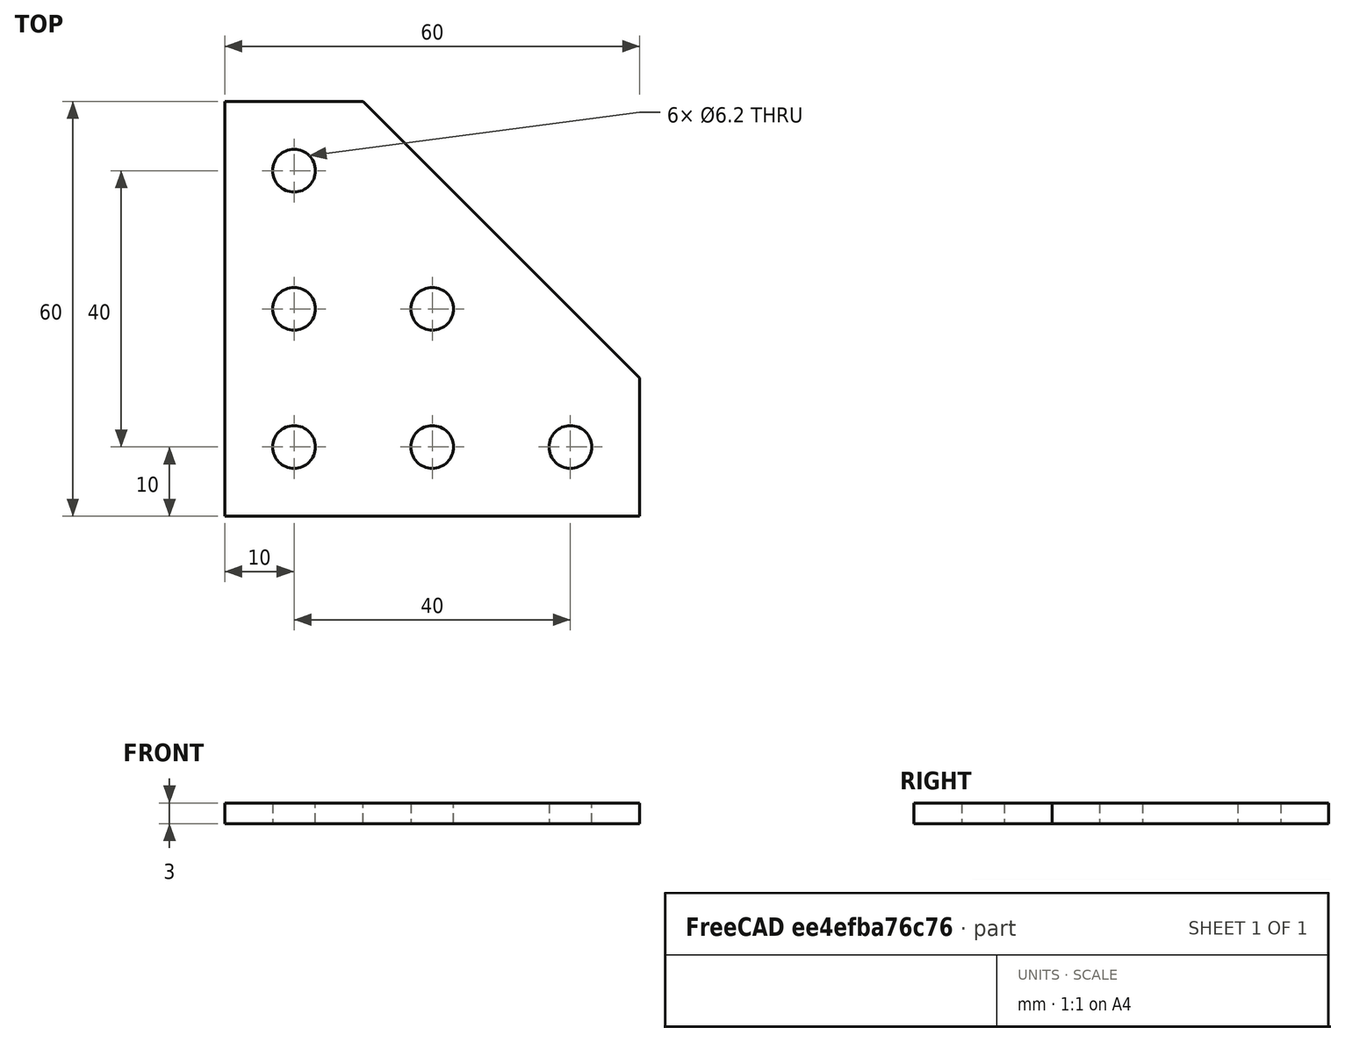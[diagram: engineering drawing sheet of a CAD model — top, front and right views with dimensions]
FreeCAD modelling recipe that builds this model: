
FCSTD DOCUMENT  (FreeCAD 0.17R9796 (Git))
Label: lcon
License: All rights reserved
LicenseURL: http://en.wikipedia.org/wiki/All_rights_reserved
objects: Sketcher::SketchObject×1, PartDesign::Pad×1, PartDesign::Body×1
note: 4 computed .brp shape members not serialized (recipe doc carries the construction recipe); baked Part::Feature solids carry a one-line shape summary decoded from their .brp

FEATURE [Sketcher::SketchObject] Sketch
  MapMode = 5
  Support = -> [XY_Plane]
  sketch-geometry (11):
    g0: LineSegment StartX=0 StartY=60 StartZ=0 EndX=20 EndY=60 EndZ=0
    g1: LineSegment StartX=20 StartY=60 StartZ=0 EndX=60 EndY=20 EndZ=0
    g2: LineSegment StartX=60 StartY=20 StartZ=0 EndX=60 EndY=0 EndZ=0
    g3: LineSegment StartX=60 StartY=0 StartZ=0 EndX=0 EndY=0 EndZ=0
    g4: LineSegment StartX=0 StartY=0 StartZ=0 EndX=0 EndY=60 EndZ=0
    g5: Circle CenterX=10 CenterY=10 CenterZ=0 NormalX=0 NormalY=0 NormalZ=1 Radius=3.1
    g6: Circle CenterX=10 CenterY=30 CenterZ=0 NormalX=0 NormalY=0 NormalZ=1 Radius=3.1
    g7: Circle CenterX=10 CenterY=50 CenterZ=0 NormalX=0 NormalY=0 NormalZ=1 Radius=3.1
    g8: Circle CenterX=30 CenterY=10 CenterZ=0 NormalX=0 NormalY=0 NormalZ=1 Radius=3.1
    g9: Circle CenterX=50 CenterY=10 CenterZ=0 NormalX=0 NormalY=0 NormalZ=1 Radius=3.1
    g10: Circle CenterX=30 CenterY=30 CenterZ=0 NormalX=0 NormalY=0 NormalZ=1 Radius=3.1
  constraints (32):
    c: Coincident(g0,g1)
    c: Coincident(g1,g2)
    c: Coincident(g2,g3)
    c: Coincident(g3,g4)
    c: Coincident(g4,g0)
    c: Coincident(g3,g-1)
    c: DistanceX(g-1,g2) = 60
    c: DistanceY(g-1,g0) = 60
    c: DistanceX(g-1,g1) = 60
    c: DistanceX(g-1,g0) = 20
    c: DistanceY(g-1,g0) = 60
    c: DistanceY(g-1,g1) = 20
    c: DistanceX(g0,g-1) = 0
    c: DistanceY(g2,g-1) = 0
    c: DistanceX(g-1,g5) = 10
    c: DistanceX(g-1,g6) = 10
    c: DistanceX(g-1,g7) = 10
    c: DistanceY(g-1,g5) = 10
    c: DistanceY(g-1,g6) = 30
    c: DistanceY(g-1,g7) = 50
    c: DistanceY(g-1,g8) = 10
    c: DistanceY(g-1,g10) = 30
    c: DistanceY(g-1,g9) = 10
    c: DistanceX(g-1,g9) = 50
    c: DistanceX(g-1,g8) = 30
    c: Radius(g7) = 3.1
    c: Radius(g6) = 3.1
    c: Radius(g10) = 3.1
    c: Radius(g5) = 3.1
    c: Radius(g8) = 3.1
    c: Radius(g9) = 3.1
    c: DistanceX(g-1,g10) = 30
FEATURE [PartDesign::Pad] Pad
  Length = 3
  Length2 = 100
  Profile = -> Sketch
  Type = 0
FEATURE [PartDesign::Body] Body
  Group = -> [Sketch,Pad]
  Origin = -> BodyOrigin
  Tip = -> Pad
